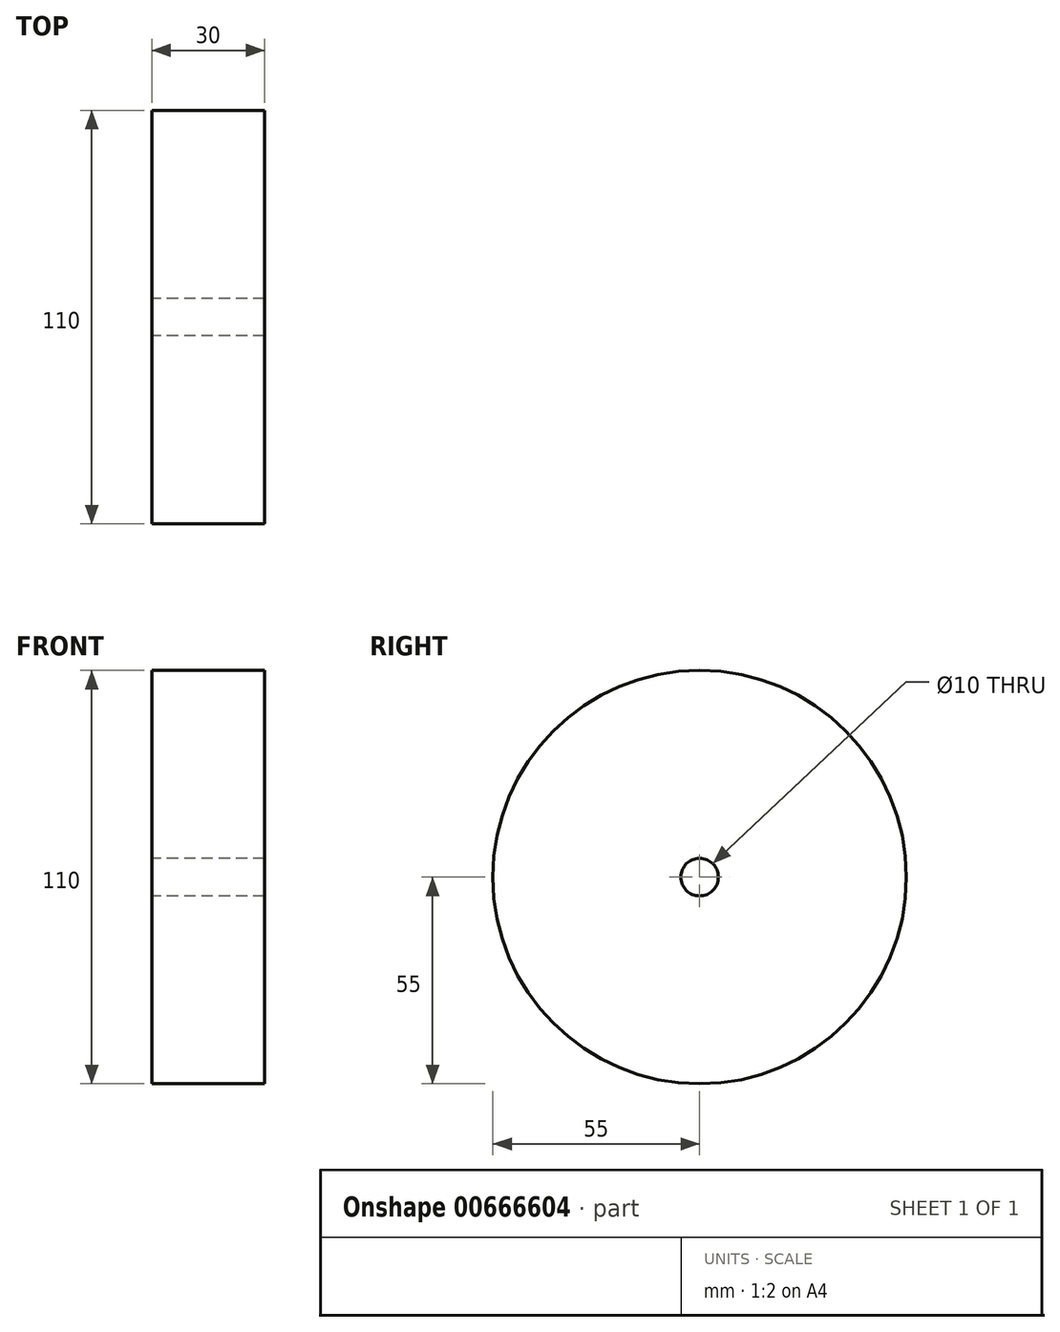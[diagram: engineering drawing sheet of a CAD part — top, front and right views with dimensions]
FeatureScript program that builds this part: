
annotation { "Feature Type Name" : "Feature", "Feature Type Description" : "" }
export const myFeature = defineFeature(function(context is Context, id is Id, definition is map)
    precondition{}
    {
        {
            var Q0;
            Q0=qCreatedBy(makeId("Right.planeOp"),FACE);
            var sketch = newSketch(context, id + "F0", { "sketchPlane" : qUnion([Q0])});
            skCircle(sketch, "E0", {"center": v(0, 0) * mm, "radius": 55 * mm});
            skCircle(sketch, "E1", {"center": v(0, 0) * mm, "radius": 5 * mm});
            skSolve(sketch);
        }
        {
            var Q0;
            Q0=makeQuery(id+"F0.imprint","IMPRINT",FACE,{"disambiguationData":[TD([[makeQuery(id+"F0.imprint","IMPRINT",EDGE,{"derivedFrom":sQuery(id+"F0.wireOp",EDGE,"E0")}),1.0]])]});
            extrude(context, id + "F1", {"entities" : qUnion([Q0]), "depth" : 30 * mm, "offsetDistance" : 25 * mm});
        }
    });
